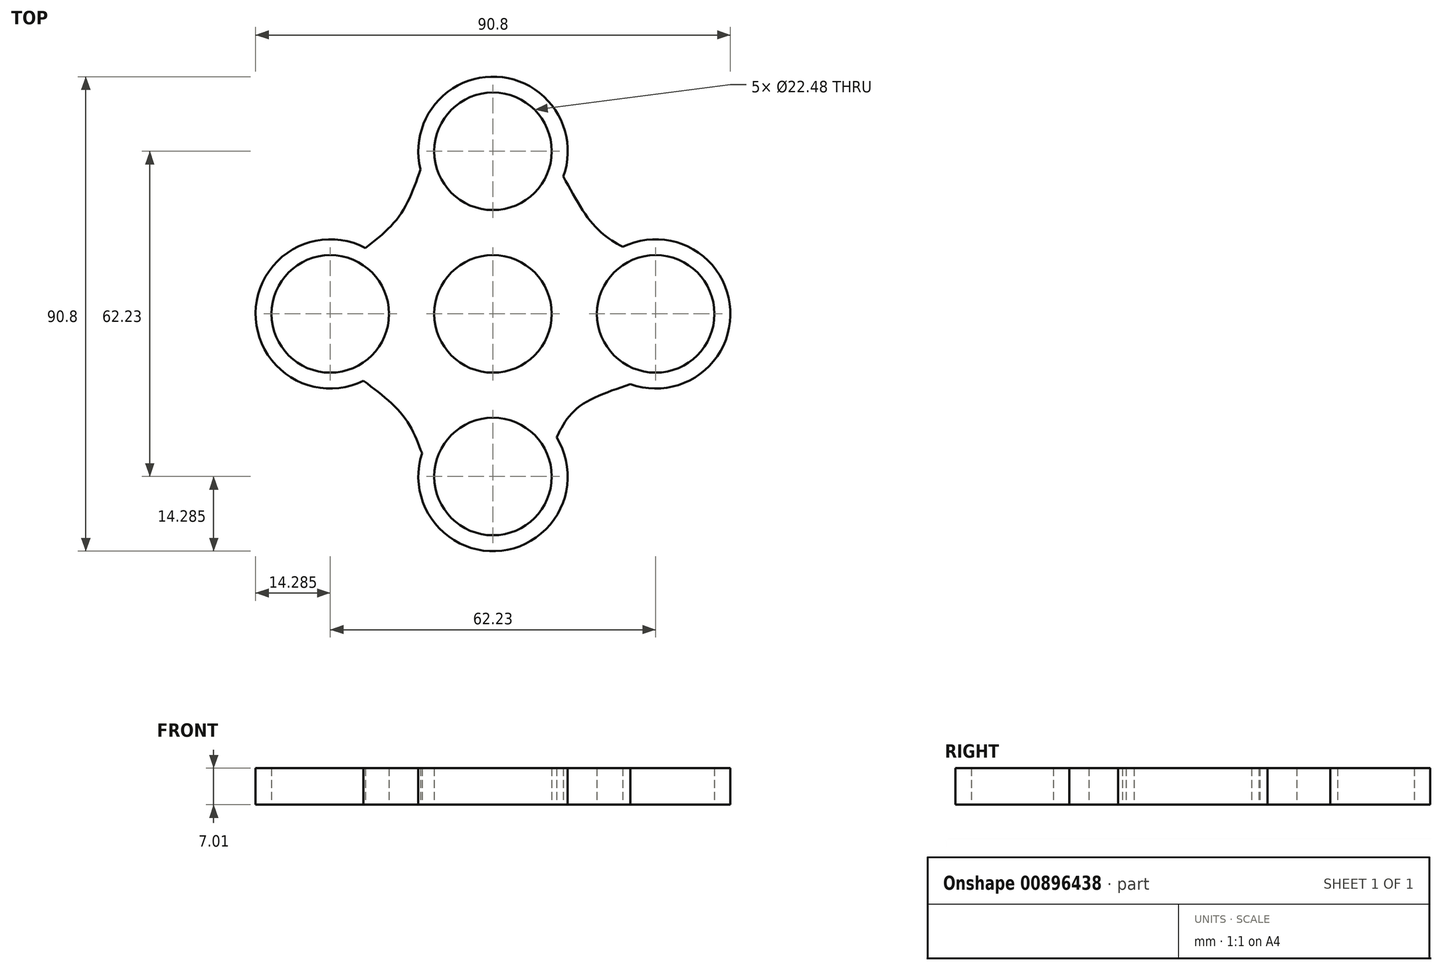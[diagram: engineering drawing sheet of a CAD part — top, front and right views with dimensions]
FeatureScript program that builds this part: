
annotation { "Feature Type Name" : "Feature", "Feature Type Description" : "" }
export const myFeature = defineFeature(function(context is Context, id is Id, definition is map)
    precondition{}
    {
        {
            var Q0;
            Q0=qCreatedBy(makeId("Top.planeOp"),FACE);
            var sketch = newSketch(context, id + "F0", { "sketchPlane" : qUnion([Q0])});
            skCircle(sketch, "E0", {"center": v(0, 0) * mm, "radius": 11.24 * mm});
            skCircle(sketch, "E1", {"center": v(0, 31.12) * mm, "radius": 11.24 * mm});
            skCircle(sketch, "E2", {"center": v(0, 0) * mm, "radius": 14.29 * mm});
            skCircle(sketch, "E3", {"center": v(0, 31.12) * mm, "radius": 14.29 * mm});
            skCircle(sketch, "E4.1.0", {"center": v(-31.12, 0) * mm, "radius": 11.24 * mm});
            skCircle(sketch, "E4.1.1", {"center": v(-31.12, 0) * mm, "radius": 14.29 * mm});
            skCircle(sketch, "E4.2.0", {"center": v(0, -31.12) * mm, "radius": 11.24 * mm});
            skCircle(sketch, "E4.2.1", {"center": v(0, -31.12) * mm, "radius": 14.29 * mm});
            skCircle(sketch, "E4.3.0", {"center": v(31.12, 0) * mm, "radius": 11.24 * mm});
            skCircle(sketch, "E4.3.1", {"center": v(31.12, 0) * mm, "radius": 14.29 * mm});
            skFitSpline(sketch, "E5", {"points": [v(-24.4, 12.61) * mm, v(-17.84, 18.84) * mm, v(-13.87, 27.67) * mm], "startDerivative": vector(14.74, 11.53) * mm, "endDerivative": vector(6.37, 18.56) * mm});
            skFitSpline(sketch, "E6", {"points": [v(-13.58, -26.66) * mm, v(-17.13, -19.6) * mm, v(-24.76, -12.8) * mm], "startDerivative": vector(-6.03, 15.67) * mm, "endDerivative": vector(-16.16, 12.17) * mm});
            skFitSpline(sketch, "E7", {"points": [v(12.15, -23.6) * mm, v(16.1, -18.03) * mm, v(26.28, -13.44) * mm], "startDerivative": vector(7.01, 13.7) * mm, "endDerivative": vector(20.7, 6.92) * mm});
            skFitSpline(sketch, "E8", {"points": [v(24.82, 12.83) * mm, v(19.7, 16.54) * mm, v(13.45, 26.3) * mm], "startDerivative": vector(-12.32, 6.94) * mm, "endDerivative": vector(-10.5, 19.36) * mm});
            skSolve(sketch);
        }
        {
            var Q0;
            Q0 = qSketchRegion(id + "F0", true);
            var Q1;
            Q1=makeQuery(id+"F0.imprint","IMPRINT",FACE,{"disambiguationData":[TD([[makeQuery(id+"F0.imprint","IMPRINT",EDGE,{"derivedFrom":sQuery(id+"F0.wireOp",EDGE,"E0")}),-1.0]])]});
            extrude(context, id + "F1", {"entities" : qUnion([Q0, Q1]), "depth" : 7 * mm, "offsetDistance" : 25.4 * mm});
        }
    });
